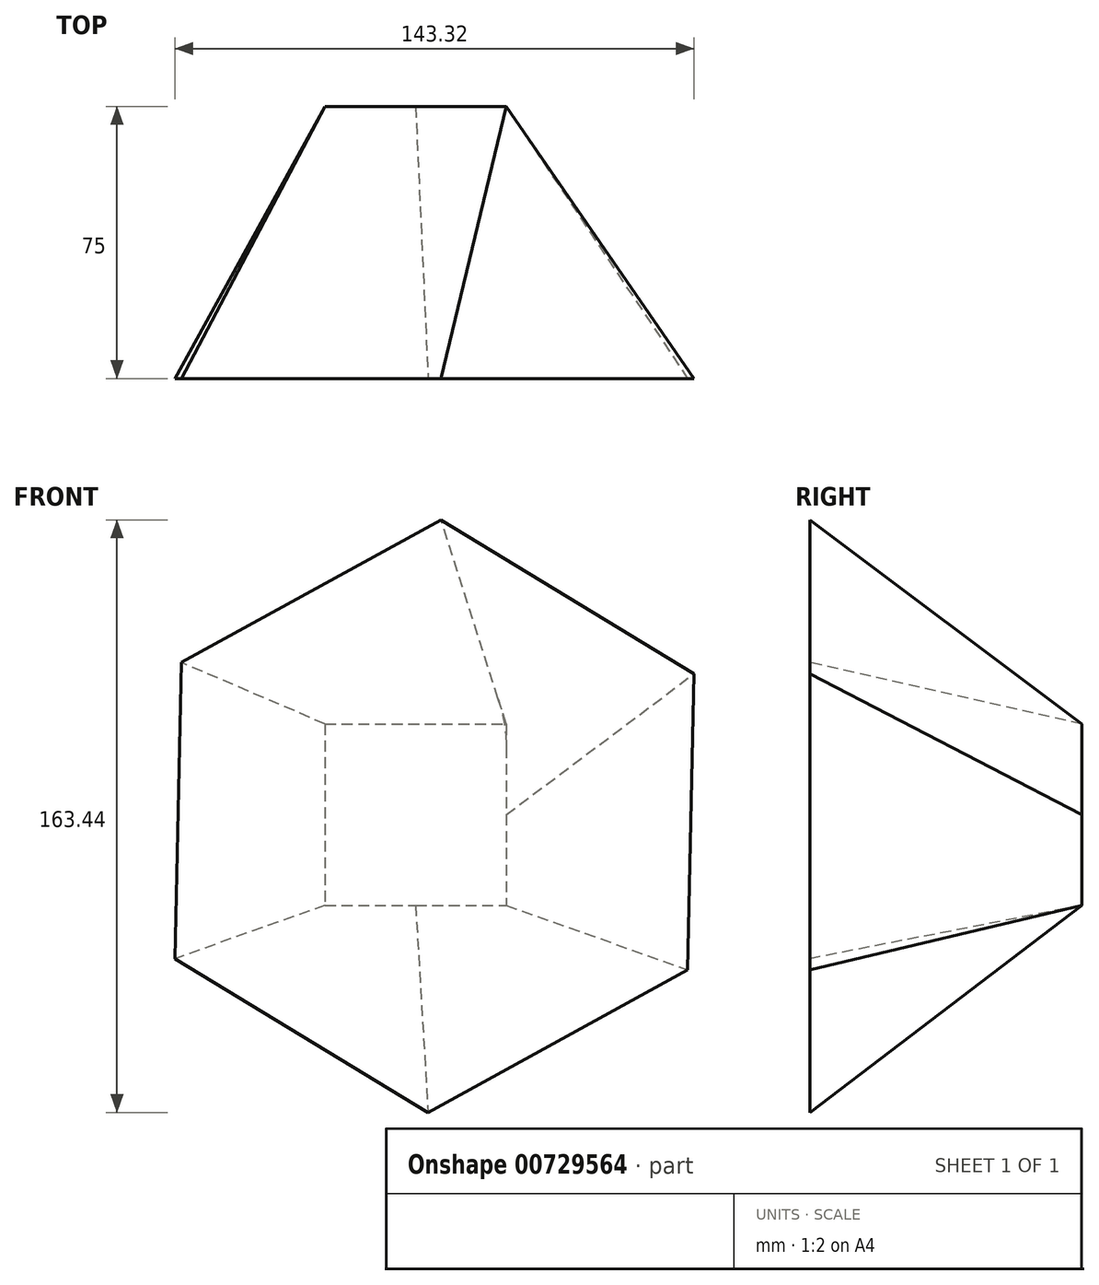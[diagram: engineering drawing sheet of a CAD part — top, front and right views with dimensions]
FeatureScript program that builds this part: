
annotation { "Feature Type Name" : "Feature", "Feature Type Description" : "" }
export const myFeature = defineFeature(function(context is Context, id is Id, definition is map)
    precondition{}
    {
        {
            var Q0;
            Q0=qCreatedBy(makeId("Front.planeOp"),FACE);
            var sketch = newSketch(context, id + "F0", { "sketchPlane" : qUnion([Q0])});
            skLineSegment(sketch, "E0.bottom", {"start": v(-26.95, 25.42) * mm, "end": v(23.05, 25.42) * mm});
            skLineSegment(sketch, "E0.top", {"start": v(-26.95, -24.58) * mm, "end": v(23.05, -24.58) * mm});
            skLineSegment(sketch, "E0.left", {"start": v(-26.95, 25.42) * mm, "end": v(-26.95, -24.58) * mm});
            skLineSegment(sketch, "E0.right", {"start": v(23.05, 25.42) * mm, "end": v(23.05, -24.58) * mm});
            skSolve(sketch);
        }
        {
            var Q0;
            Q0=qCreatedBy(makeId("Front.planeOp"),FACE);
            cPlane(context, id + "F1", {"entities" : qUnion([Q0]), "cplaneType" : CPlaneType.OFFSET, "offset" : 50 * mm, "width" : 150 * mm, "height" : 150 * mm});
        }
        {
            var Q0;
            Q0=qCreatedBy(id+"F1.planeOp",FACE);
            cPlane(context, id + "F2", {"entities" : qUnion([Q0]), "cplaneType" : CPlaneType.OFFSET, "offset" : 25 * mm, "width" : 150 * mm, "height" : 150 * mm});
        }
        {
            var Q0;
            Q0=qCreatedBy(id+"F2.planeOp",FACE);
            var sketch = newSketch(context, id + "F3", { "sketchPlane" : qUnion([Q0])});
            skCircle(sketch, "E1.cCircle", {"center": v(3.3, 0) * mm, "radius": 81.74 * mm, "construction": true});
            skLineSegment(sketch, "E1.0", {"start": v(74.95, 39.32) * mm, "end": v(73.17, -42.4) * mm});
            skLineSegment(sketch, "E1.1", {"start": v(73.17, -42.4) * mm, "end": v(1.51, -81.72) * mm});
            skLineSegment(sketch, "E1.2", {"start": v(1.51, -81.72) * mm, "end": v(-68.37, -39.32) * mm});
            skLineSegment(sketch, "E1.3", {"start": v(-68.37, -39.32) * mm, "end": v(-66.59, 42.4) * mm});
            skLineSegment(sketch, "E1.4", {"start": v(-66.59, 42.4) * mm, "end": v(5.07, 81.72) * mm});
            skLineSegment(sketch, "E1.5", {"start": v(5.07, 81.72) * mm, "end": v(74.95, 39.32) * mm});
            skSolve(sketch);
        }
        {
            var Q0;
            Q0=makeQuery(id+"F0.imprint","IMPRINT",FACE,{"disambiguationData":[TD([[makeQuery(id+"F0.imprint","IMPRINT",EDGE,{"derivedFrom":sQuery(id+"F0.wireOp",EDGE,"E0.bottom")}),-1.0]])]});
            var Q1;
            Q1=makeQuery(id+"F3.imprint","IMPRINT",FACE,{"disambiguationData":[TD([[makeQuery(id+"F3.imprint","IMPRINT",EDGE,{"derivedFrom":sQuery(id+"F3.wireOp",EDGE,"E1.0")}),-1.0]])]});
            loft(context, id + "F4", {"sheetProfilesArray" : [{ "sheetProfileEntities" : qUnion([Q0]) }, { "sheetProfileEntities" : qUnion([Q1]) }]});
        }
    });
